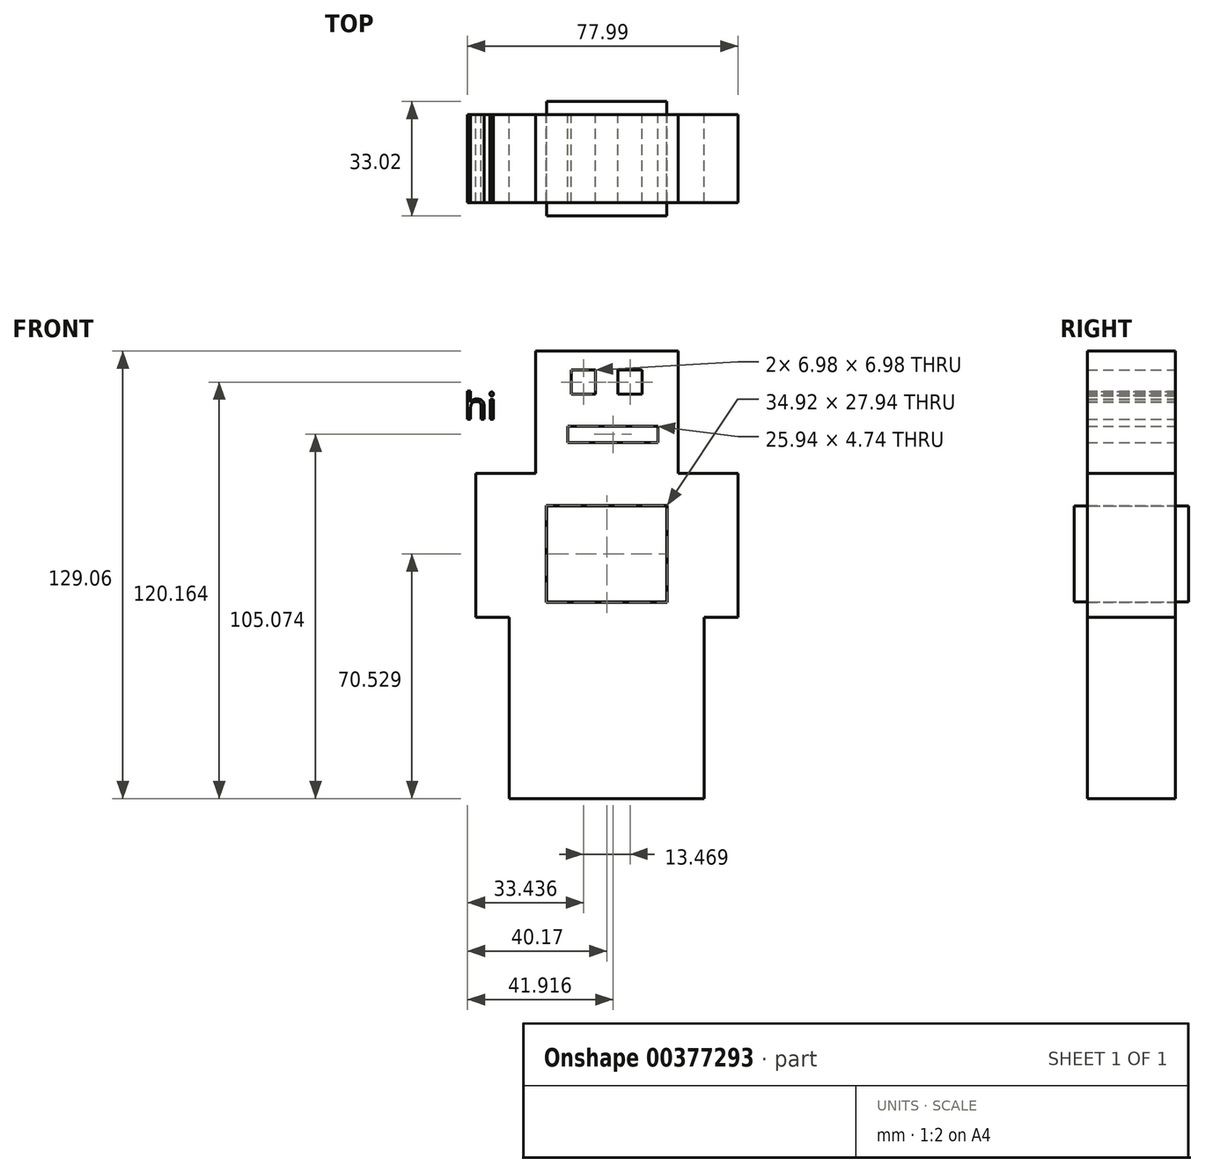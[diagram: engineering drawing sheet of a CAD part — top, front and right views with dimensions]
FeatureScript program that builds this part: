
annotation { "Feature Type Name" : "Feature", "Feature Type Description" : "" }
export const myFeature = defineFeature(function(context is Context, id is Id, definition is map)
    precondition{}
    {
        {
            var Q0;
            Q0=qCreatedBy(makeId("Front.planeOp"),FACE);
            var sketch = newSketch(context, id + "F0", { "sketchPlane" : qUnion([Q0])});
            skLineSegment(sketch, "E0", {"start": v(0, 41.48) * mm, "end": v(20.57, 41.48) * mm});
            skLineSegment(sketch, "E1", {"start": v(20.57, 41.48) * mm, "end": v(20.57, 76.78) * mm});
            skLineSegment(sketch, "E2", {"start": v(20.57, 41.48) * mm, "end": v(37.82, 41.48) * mm});
            skLineSegment(sketch, "E3", {"start": v(37.82, 41.48) * mm, "end": v(37.82, 0) * mm});
            skLineSegment(sketch, "E4", {"start": v(37.82, 0) * mm, "end": v(25.96, 0) * mm});
            skLineSegment(sketch, "E5", {"start": v(25.96, 0) * mm, "end": v(25.96, 28.55) * mm});
            skLineSegment(sketch, "E6", {"start": v(28.12, 0) * mm, "end": v(28.12, -52.28) * mm});
            skLineSegment(sketch, "E7", {"start": v(28.12, -52.28) * mm, "end": v(0, -52.28) * mm});
            skLineSegment(sketch, "E8", {"start": v(28.12, -44.73) * mm, "end": v(0, -44.73) * mm});
            skLineSegment(sketch, "E9.MirrorCS", {"start": v(-20.57, 41.48) * mm, "end": v(-20.57, 76.78) * mm});
            skLineSegment(sketch, "E10.MirrorCS", {"start": v(0, 41.48) * mm, "end": v(-20.57, 41.48) * mm});
            skLineSegment(sketch, "E11.MirrorCS", {"start": v(-20.57, 41.48) * mm, "end": v(-37.82, 41.48) * mm});
            skLineSegment(sketch, "E12.MirrorCS", {"start": v(-37.82, 41.48) * mm, "end": v(-37.82, 0) * mm});
            skLineSegment(sketch, "E13.MirrorCS", {"start": v(-25.96, 0) * mm, "end": v(-25.96, 28.55) * mm});
            skLineSegment(sketch, "E14.MirrorCS", {"start": v(-37.82, 0) * mm, "end": v(-25.96, 0) * mm});
            skLineSegment(sketch, "E15.MirrorCS", {"start": v(-28.12, 0) * mm, "end": v(-28.12, -52.28) * mm});
            skLineSegment(sketch, "E16.MirrorCS", {"start": v(-28.12, -44.73) * mm, "end": v(0, -44.73) * mm});
            skLineSegment(sketch, "E17.MirrorCS", {"start": v(-28.12, -52.28) * mm, "end": v(0, -52.28) * mm});
            skPoint(sketch, "E18.MirrorCS.end.orphan", {"position": v(-20.57, 76.78) * mm});
            skLineSegment(sketch, "E19", {"start": v(-20.57, 76.78) * mm, "end": v(20.57, 76.78) * mm});
            skLineSegment(sketch, "E20", {"start": v(14.72, 55.16) * mm, "end": v(-11.22, 55.16) * mm});
            skLineSegment(sketch, "E21", {"start": v(-11.22, 55.16) * mm, "end": v(-11.22, 50.42) * mm});
            skLineSegment(sketch, "E22", {"start": v(-11.22, 50.42) * mm, "end": v(14.72, 50.42) * mm});
            skLineSegment(sketch, "E23", {"start": v(14.72, 55.16) * mm, "end": v(14.72, 50.42) * mm});
            skLineSegment(sketch, "E24", {"start": v(-3.24, 71.38) * mm, "end": v(-10.23, 71.38) * mm});
            skLineSegment(sketch, "E25", {"start": v(-10.23, 71.38) * mm, "end": v(-10.23, 64.4) * mm});
            skLineSegment(sketch, "E26", {"start": v(-10.23, 64.4) * mm, "end": v(-3.24, 64.4) * mm});
            skLineSegment(sketch, "E27", {"start": v(-3.24, 64.4) * mm, "end": v(-3.24, 71.38) * mm});
            skPoint(sketch, "E28.orphan", {"position": v(-3.24, 71.38) * mm});
            skPoint(sketch, "E29.orphan", {"position": v(-10.23, 71.38) * mm});
            skLineSegment(sketch, "E30.MirrorCS", {"start": v(3.24, 64.4) * mm, "end": v(3.24, 71.38) * mm});
            skPoint(sketch, "E31.MirrorP", {"position": v(3.24, 71.38) * mm});
            skLineSegment(sketch, "E32.MirrorCS", {"start": v(3.24, 71.38) * mm, "end": v(10.23, 71.38) * mm});
            skLineSegment(sketch, "E33.MirrorCS", {"start": v(10.23, 71.38) * mm, "end": v(10.23, 64.4) * mm});
            skLineSegment(sketch, "E34.MirrorCS", {"start": v(10.23, 64.4) * mm, "end": v(3.24, 64.4) * mm});
            skPoint(sketch, "E35.MirrorP", {"position": v(10.23, 71.38) * mm});
            skLineSegment(sketch, "E36.bottom", {"start": v(-17.46, 32.22) * mm, "end": v(17.46, 32.22) * mm});
            skLineSegment(sketch, "E36.top", {"start": v(-17.46, 4.28) * mm, "end": v(17.46, 4.28) * mm});
            skLineSegment(sketch, "E36.left", {"start": v(-17.46, 32.22) * mm, "end": v(-17.46, 4.28) * mm});
            skLineSegment(sketch, "E36.right", {"start": v(17.46, 32.22) * mm, "end": v(17.46, 4.28) * mm});
            skPoint(sketch, "E36.middle", {"position": v(0, 18.25) * mm});
            skCircle(sketch, "E37", {"center": v(-10.57, 24.48) * mm, "radius": 3.22 * mm});
            skCircle(sketch, "E38.MirrorC", {"center": v(10.57, 24.48) * mm, "radius": 3.22 * mm});
            skCircle(sketch, "E39", {"center": v(0, 24.48) * mm, "radius": 3.22 * mm});
            skText(sketch, "E40", { "text": "hi", "fontName": "OpenSans-Regular.ttf"});
            const initialGuessF0  = {"E40": [-0.04108, 0.05721, 1, 0, 0.00765]};
            skSetInitialGuess(sketch, initialGuessF0);
            skSolve(sketch);
        }
        {
            var Q0;
            Q0 = qSketchRegion(id + "F0", true);
            extrude(context, id + "F1", {"entities" : qUnion([Q0]), "endBound" : BoundingType.SYMMETRIC, "depth" : 25.4 * mm, "offsetDistance" : 25.4 * mm});
        }
        {
            var Q0;
            Q0=qCreatedBy(makeId("Front.planeOp"),FACE);
            var sketch = newSketch(context, id + "F2", { "sketchPlane" : qUnion([Q0])});
            skLineSegment(sketch, "E41.0.0", {"start": v(28.12, -52.28) * mm, "end": v(28.12, 0) * mm});
            skLineSegment(sketch, "E41.0.1", {"start": v(28.12, 0) * mm, "end": v(37.82, 0) * mm});
            skLineSegment(sketch, "E41.0.2", {"start": v(37.82, 0) * mm, "end": v(37.82, 41.48) * mm});
            skLineSegment(sketch, "E41.0.3", {"start": v(37.82, 41.48) * mm, "end": v(20.57, 41.48) * mm});
            skLineSegment(sketch, "E41.0.4", {"start": v(20.57, 41.48) * mm, "end": v(20.57, 76.78) * mm});
            skLineSegment(sketch, "E41.0.5", {"start": v(20.57, 76.78) * mm, "end": v(-20.57, 76.78) * mm});
            skLineSegment(sketch, "E41.0.6", {"start": v(-20.57, 76.78) * mm, "end": v(-20.57, 41.48) * mm});
            skLineSegment(sketch, "E41.0.7", {"start": v(-20.57, 41.48) * mm, "end": v(-37.82, 41.48) * mm});
            skLineSegment(sketch, "E41.0.8", {"start": v(-37.82, 41.48) * mm, "end": v(-37.82, 0) * mm});
            skLineSegment(sketch, "E41.0.9", {"start": v(-37.82, 0) * mm, "end": v(-28.12, 0) * mm});
            skLineSegment(sketch, "E41.0.10", {"start": v(-28.12, 0) * mm, "end": v(-28.12, -52.28) * mm});
            skLineSegment(sketch, "E41.0.11", {"start": v(-28.12, -52.28) * mm, "end": v(28.12, -52.28) * mm});
            skLineSegment(sketch, "E42.0", {"start": v(-17.33, 32.09) * mm, "end": v(-17.33, 4.4) * mm});
            skLineSegment(sketch, "E42.1", {"start": v(-17.33, 32.09) * mm, "end": v(17.33, 32.09) * mm});
            skLineSegment(sketch, "E42.2", {"start": v(17.33, 32.09) * mm, "end": v(17.33, 4.4) * mm});
            skLineSegment(sketch, "E42.3", {"start": v(-17.33, 4.4) * mm, "end": v(17.33, 4.4) * mm});
            skSolve(sketch);
        }
        {
            var Q0;
            Q0=makeQuery(id+"F2.imprint","IMPRINT",FACE,{"disambiguationData":[TD([[makeQuery(id+"F2.imprint","IMPRINT",EDGE,{"derivedFrom":sQuery(id+"F2.wireOp",EDGE,"E42.0")}),1.0]])]});
            extrude(context, id + "F3", {"entities" : qUnion([Q0]), "endBound" : BoundingType.SYMMETRIC, "depth" : 33.02 * mm, "offsetDistance" : 25.4 * mm});
        }
        {
            var Q0;
            Q0=qCreatedBy(makeId("Front.planeOp"),FACE);
            var sketch = newSketch(context, id + "F4", { "sketchPlane" : qUnion([Q0])});
            skCircle(sketch, "E43", {"center": v(-11.57, 25.33) * mm, "radius": 4.19 * mm});
            skCircle(sketch, "E44", {"center": v(0, 25.33) * mm, "radius": 4.19 * mm});
            skCircle(sketch, "E45", {"center": v(11.19, 25.33) * mm, "radius": 4.19 * mm});
            skLineSegment(sketch, "E46.bottom", {"start": v(-11.57, 19.19) * mm, "end": v(11.19, 19.19) * mm});
            skLineSegment(sketch, "E46.top", {"start": v(-11.57, 15.66) * mm, "end": v(11.19, 15.66) * mm});
            skLineSegment(sketch, "E46.left", {"start": v(-11.57, 19.19) * mm, "end": v(-11.57, 15.66) * mm});
            skLineSegment(sketch, "E46.right", {"start": v(11.19, 19.19) * mm, "end": v(11.19, 15.66) * mm});
            skSolve(sketch);
        }
        {
            var Q0;
            Q0 = qSketchRegion(id + "F4", true);
            extrude(context, id + "F5", {"entities" : qUnion([Q0]), "operationType" : NewBodyOperationType.ADD, "oppositeDirection" : true, "depth" : 12.2 * mm, "offsetDistance" : 25.4 * mm});
        }
    });
